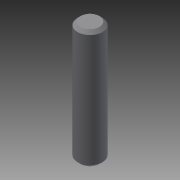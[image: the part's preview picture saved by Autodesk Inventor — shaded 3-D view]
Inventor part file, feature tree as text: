
AUTODESK INVENTOR PART (.ipt)
format: ipt  version: 2014 SP2 (Build 180246200, 246)  size: 134,656 bytes
history: native  units: in
note: dims shown in document units (in); Inventor stores cm internally (conversion verified against a paired STEP export)
features: other x112, revolve x1, sketch x1
ambient origin geometry x8: Origin, YZ Plane, XZ Plane, XY Plane, X Axis, Y Axis, Z Axis, Center Point
bodies: Solid1 (feature_tree)
feature tree (114):
  revolve  "Revolution1"  [1 undecoded]
  other  "b11_XY"
  other  "b11_YZ"
  other  "b11_ZX"
  other  "b11_X"
  other  "b11_Y"
  other  "b11_Z"
  other  "b11_Center"
  other  "b2_XY"
  other  "b2_YZ"
  other  "b2_ZX"
  other  "b2_X"
  other  "b2_Y"
  other  "b2_Z"
  other  "b2_Center"
  other  "f1_XY"
  other  "f1_YZ"
  other  "f1_ZX"
  other  "f1_X"
  other  "f1_Y"
  other  "f1_Z"
  other  "f1_Center"
  other  "f2_XY"
  other  "f2_YZ"
  other  "f2_ZX"
  other  "f2_X"
  other  "f2_Y"
  other  "f2_Z"
  other  "f2_Center"
  other  "h1_XY"
  other  "h1_YZ"
  other  "h1_ZX"
  other  "h1_X"
  other  "h1_Y"
  other  "h1_Z"
  other  "h1_Center"
  other  "h2_XY"
  other  "h2_YZ"
  other  "h2_ZX"
  other  "h2_X"
  other  "h2_Y"
  other  "h2_Z"
  other  "h2_Center"
  other  "npt1_XY"
  other  "npt1_YZ"
  other  "npt1_ZX"
  other  "npt1_X"
  other  "npt1_Y"
  other  "npt1_Z"
  other  "npt1_Center"
  other  "npt1_1_XY"
  other  "npt1_1_YZ"
  other  "npt1_1_ZX"
  other  "npt1_1_X"
  other  "npt1_1_Y"
  other  "npt1_1_Z"
  other  "npt1_1_Center"
  other  "npt2_XY"
  other  "npt2_YZ"
  other  "npt2_ZX"
  other  "npt2_X"
  other  "npt2_Y"
  other  "npt2_Z"
  other  "npt2_Center"
  other  "npt2_1_XY"
  other  "npt2_1_YZ"
  other  "npt2_1_ZX"
  other  "npt2_1_X"
  other  "npt2_1_Y"
  other  "npt2_1_Z"
  other  "npt2_1_Center"
  other  "rod_XY"
  other  "rod_YZ"
  other  "rod_ZX"
  other  "rod_X"
  other  "rod_Y"
  other  "rod_Z"
  other  "rod_Center"
  other  "rod_to_part_XY"
  other  "rod_to_part_YZ"
  other  "rod_to_part_ZX"
  other  "rod_to_part_X"
  other  "rod_to_part_Y"
  other  "rod_to_part_Z"
  other  "rod_to_part_Center"
  other  "th1_XY"
  other  "th1_YZ"
  other  "th1_ZX"
  other  "th1_X"
  other  "th1_Y"
  other  "th1_Z"
  other  "th1_Center"
  other  "th2_XY"
  other  "th2_YZ"
  other  "th2_ZX"
  other  "th2_X"
  other  "th2_Y"
  other  "th2_Z"
  other  "th2_Center"
  other  "to_rod_pivot_XY"
  other  "to_rod_pivot_YZ"
  other  "to_rod_pivot_ZX"
  other  "to_rod_pivot_X"
  other  "to_rod_pivot_Y"
  other  "to_rod_pivot_Z"
  other  "to_rod_pivot_Center"
  other  "to_rod_pivot1_XY"
  other  "to_rod_pivot1_YZ"
  other  "to_rod_pivot1_ZX"
  other  "to_rod_pivot1_X"
  other  "to_rod_pivot1_Y"
  other  "to_rod_pivot1_Z"
  other  "to_rod_pivot1_Center"
  sketch  "Sketch_10"  dims[d0=360.0deg d1=0.0in d2=0.0in d3=0.0in d4=0.0in d5=0.0in d6=0.0in d7=0.0in d8=0.0in d9=0.0in d10=0.0in d11=0.0in d12=0.0in]
note: 1 required parameter value undecoded (feature->parameter linkage not recoverable at this tier; creation-order binding heuristic only, values carry confidence <= 0.55)
